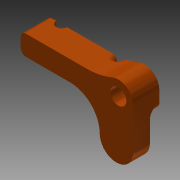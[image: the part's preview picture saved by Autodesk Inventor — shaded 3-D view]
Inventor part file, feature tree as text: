
AUTODESK INVENTOR PART (.ipt)
format: ipt  version: 2013 (Build 170138000, 138)  size: 196,096 bytes
history: native  units: in
note: dims shown in document units (in); Inventor stores cm internally (conversion verified against a paired STEP export)
features: sketch x7, other x2, extrude x1
ambient origin geometry x8: Origin, YZ Plane, XZ Plane, XY Plane, X Axis, Y Axis, Z Axis, Center Point
bodies: Solid1 (feature_tree)
feature tree (10):
  extrude  "EXTRUDER ARM.ipt"  [1 undecoded]
  other  "Solid1::EXTRUDER ARM.ipt"
  other  "TaggingFeature1"
  sketch  "Sketch1"  dims[d0=0.3937in]
  sketch  "Sketch2"  dims[d3=0.4331in d5=0.8287in d6=0.2953in d7=0.9843in d8=0.8268in d9=0.3858in d10=0.0in d12=0.0in d13=0.7874in d16=0.189in d17=0.0984in d18=0.0in d19=0.4134in d23=0.0394in d24=0.0in d25=0.0787in d26=0.0787in d27=0.1575in d30=0.0in d31=0.2205in d34=0.0394in d35=0.0in d36=0.0787in d38=0.0in d39=0.0787in d40=0.0787in d43=0.0039in]
  sketch  "Sketch3"
  sketch  "Sketch4"
  sketch  "Sketch5"
  sketch  "Sketch6"
  sketch  "Sketch7"
note: 1 required parameter value undecoded (feature->parameter linkage not recoverable at this tier; creation-order binding heuristic only, values carry confidence <= 0.55)
